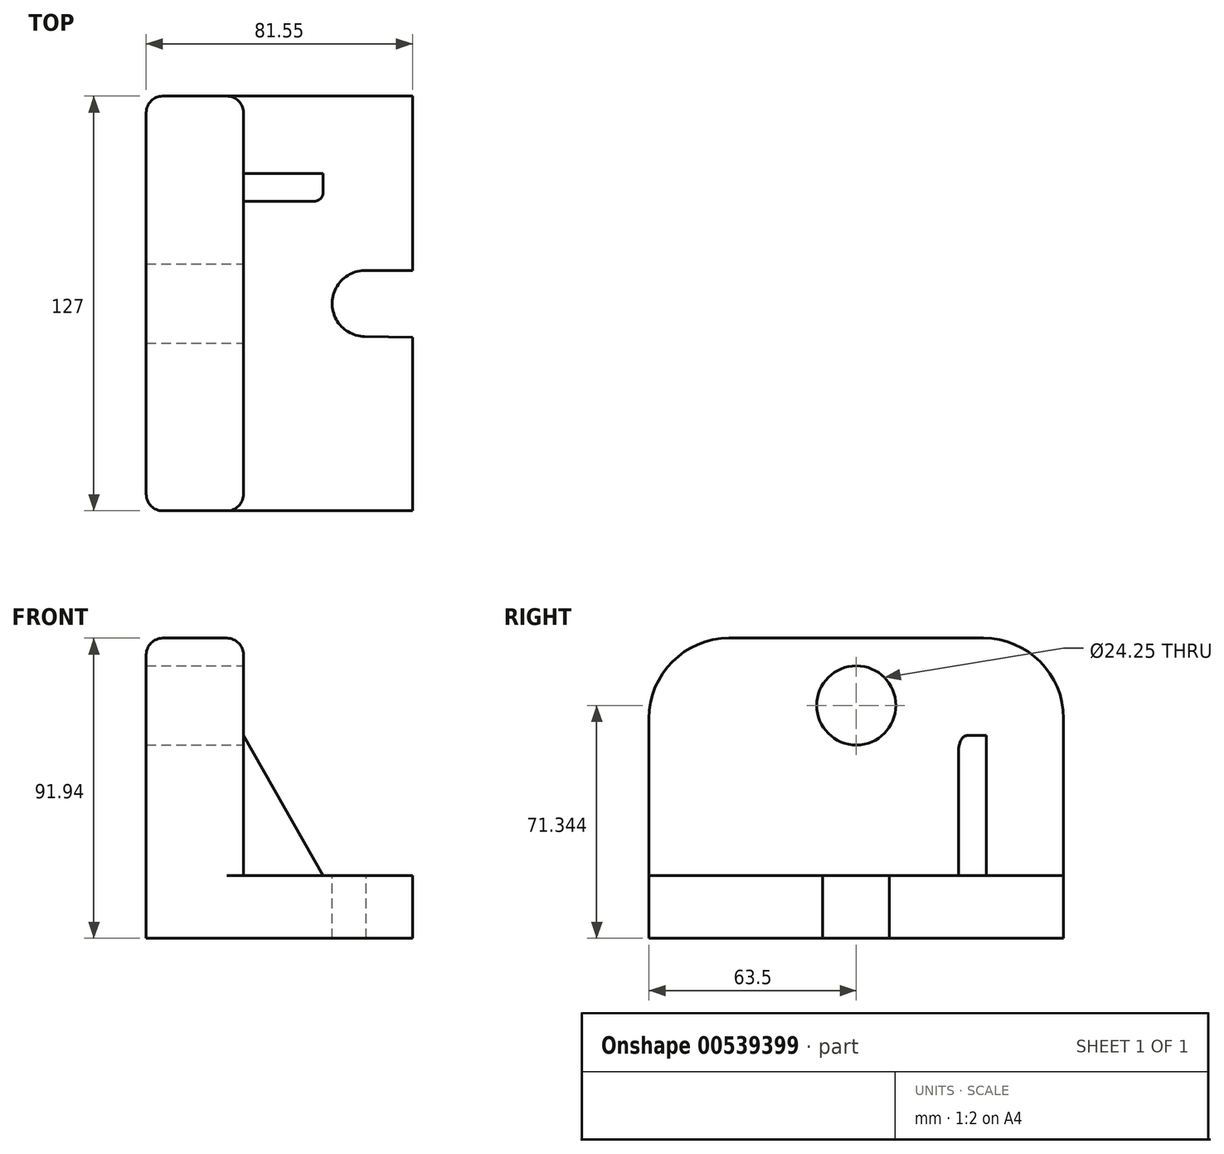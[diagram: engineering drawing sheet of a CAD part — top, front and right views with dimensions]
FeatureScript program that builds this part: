
annotation { "Feature Type Name" : "Feature", "Feature Type Description" : "" }
export const myFeature = defineFeature(function(context is Context, id is Id, definition is map)
    precondition{}
    {
        {
            var Q0;
            Q0=qCreatedBy(makeId("Front.planeOp"),FACE);
            var sketch = newSketch(context, id + "F0", { "sketchPlane" : qUnion([Q0])});
            skLineSegment(sketch, "E0", {"start": v(0, -21.47) * mm, "end": v(51.77, -21.47) * mm});
            skLineSegment(sketch, "E1", {"start": v(51.77, -21.47) * mm, "end": v(51.77, -40.63) * mm});
            skLineSegment(sketch, "E2", {"start": v(51.77, -40.63) * mm, "end": v(-29.78, -40.63) * mm});
            skLineSegment(sketch, "E3", {"start": v(-29.78, -40.63) * mm, "end": v(-29.78, 51.3) * mm});
            skLineSegment(sketch, "E4", {"start": v(-29.78, 51.3) * mm, "end": v(0, 51.3) * mm});
            skLineSegment(sketch, "E5", {"start": v(0, 51.3) * mm, "end": v(0, -21.47) * mm});
            skSolve(sketch);
        }
        {
            var Q0;
            Q0 = qSketchRegion(id + "F0", true);
            extrude(context, id + "F1", {"entities" : qUnion([Q0]), "endBound" : BoundingType.SYMMETRIC, "oppositeDirection" : true, "depth" : 127 * mm, "offsetDistance" : 25.4 * mm});
        }
        {
            var Q0;
            Q0=makeQuery(id+"F1.opExtrude","SWEPT_FACE",FACE,{"disambiguationData":[OSD([sQuery(id+"F0.wireOp",EDGE,"E0")])]});
            var sketch = newSketch(context, id + "F2", { "sketchPlane" : qUnion([Q0])});
            skPoint(sketch, "E6.centerSnap0", {"position": v(51.77, 0) * mm});
            skCircle(sketch, "E7", {"center": v(37.28, 0) * mm, "radius": 10.1 * mm});
            skLineSegment(sketch, "E8", {"start": v(36.9, 10.1) * mm, "end": v(51.77, 10.1) * mm});
            skLineSegment(sketch, "E9", {"start": v(37.13, -10.1) * mm, "end": v(51.77, -10.32) * mm});
            skSolve(sketch);
        }
        {
            var Q0;
            Q0 = qSketchRegion(id + "F2", true);
            var Q1;
            {var subQ0=sQuery(id+"F2.wireOp",EDGE,"E9");Q1=makeQuery(id+"F2.imprint","IMPRINT",FACE,{"disambiguationData":[TD([[makeQuery(id+"F2.imprint","IMPRINT",EDGE,{"derivedFrom":subQ0}),1.0]])]});}
            extrude(context, id + "F3", {"entities" : qUnion([Q0, Q1]), "operationType" : NewBodyOperationType.REMOVE, "oppositeDirection" : true, "depth" : 79.5 * mm, "offsetDistance" : 25.4 * mm});
        }
        {
            var Q0;
            Q0=makeQuery(id+"F1.opExtrude","CAP_EDGE",EDGE,{"disambiguationData":[OSD([sQuery(id+"F0.wireOp",EDGE,"E4")])],"isStart":true});
            var Q1;
            Q1=makeQuery(id+"F1.opExtrude","CAP_EDGE",EDGE,{"disambiguationData":[OSD([sQuery(id+"F0.wireOp",EDGE,"E4")])],"isStart":false});
            fillet(context, id + "F4", {"entities" : qUnion([Q0, Q1]), "radius" : 24.53 * mm, "tangentPropagation" : true, "allowEdgeOverflow" : false});
        }
        {
            var Q0;
            Q0=makeQuery(id+"F1.opExtrude","SWEPT_EDGE",EDGE,{"disambiguationData":[OSD([sQuery(id+"F0.wireOp",EDGE,"E4"),sQuery(id+"F0.wireOp",EDGE,"E5")])]});
            var Q1;
            Q1=makeQuery(id+"F1.opExtrude","SWEPT_EDGE",EDGE,{"disambiguationData":[OSD([sQuery(id+"F0.wireOp",EDGE,"E3"),sQuery(id+"F0.wireOp",EDGE,"E4")])]});
            fillet(context, id + "F5", {"entities" : qUnion([Q0, Q1]), "radius" : 5.08 * mm, "tangentPropagation" : true, "allowEdgeOverflow" : false});
        }
        {
            var Q0;
            Q0=qCreatedBy(makeId("Right.planeOp"),FACE);
            var sketch = newSketch(context, id + "F6", { "sketchPlane" : qUnion([Q0])});
            skCircle(sketch, "E10", {"center": v(0, 30.71) * mm, "radius": 12.13 * mm});
            skSolve(sketch);
        }
        {
            var Q0;
            Q0 = qSketchRegion(id + "F6", true);
            extrude(context, id + "F7", {"entities" : qUnion([Q0]), "operationType" : NewBodyOperationType.REMOVE, "oppositeDirection" : true, "depth" : 116.84 * mm, "offsetDistance" : 25.4 * mm});
        }
        {
            var Q0;
            Q0=makeQuery(id+"F1.opExtrude","SWEPT_FACE",FACE,{"disambiguationData":[OSD([sQuery(id+"F0.wireOp",EDGE,"E5")])]});
            var sketch = newSketch(context, id + "F8", { "sketchPlane" : qUnion([Q0])});
            skLineSegment(sketch, "E11.bottom", {"start": v(39.8, -21.47) * mm, "end": v(31.3, -21.47) * mm});
            skLineSegment(sketch, "E11.top", {"start": v(39.8, 21.47) * mm, "end": v(31.3, 21.47) * mm});
            skLineSegment(sketch, "E11.left", {"start": v(39.8, -21.47) * mm, "end": v(39.8, 21.47) * mm});
            skLineSegment(sketch, "E11.right", {"start": v(31.3, -21.47) * mm, "end": v(31.3, 21.47) * mm});
            skPoint(sketch, "E11.middle", {"position": v(35.54, 0) * mm});
            skLineSegment(sketch, "E12.MirrorCS", {"start": v(-31.3, -21.47) * mm, "end": v(-31.3, 21.47) * mm});
            skLineSegment(sketch, "E13.MirrorCS", {"start": v(-39.8, -21.47) * mm, "end": v(-39.8, 21.47) * mm});
            skLineSegment(sketch, "E14.MirrorCS", {"start": v(-39.8, 21.47) * mm, "end": v(-31.3, 21.47) * mm});
            skSolve(sketch);
        }
        {
            var Q0;
            Q0 = qSketchRegion(id + "F8", true);
            extrude(context, id + "F9", {"entities" : qUnion([Q0]), "operationType" : NewBodyOperationType.ADD, "depth" : 24.38 * mm, "offsetDistance" : 25.4 * mm});
        }
        {
            var Q0;
            Q0=makeQuery(id+"F9.opExtrude","SWEPT_FACE",FACE,{"disambiguationData":[OSD([sQuery(id+"F8.wireOp",EDGE,"E11.left")])]});
            var sketch = newSketch(context, id + "F10", { "sketchPlane" : qUnion([Q0])});
            skLineSegment(sketch, "E15", {"start": v(0, 21.47) * mm, "end": v(-24.38, -21.47) * mm});
            skSolve(sketch);
        }
        {
            var Q0;
            Q0=makeQuery(id+"F10.imprint","IMPRINT",FACE,{"disambiguationData":[TD([[makeQuery(id+"F10.imprint","IMPRINT",EDGE,{"derivedFrom":sQuery(id+"F10.wireOp",EDGE,"E15")}),-1.0]])]});
            extrude(context, id + "F11", {"entities" : qUnion([Q0]), "operationType" : NewBodyOperationType.REMOVE, "oppositeDirection" : true, "depth" : 99.82 * mm, "offsetDistance" : 25.4 * mm});
        }
        {
            var Q0;
            Q0=makeQuery(id+"F9.opExtrude","CAP_EDGE",EDGE,{"disambiguationData":[OSD([sQuery(id+"F8.wireOp",EDGE,"E11.left")])],"isStart":true});
            var Q1;
            Q1=makeQuery(id+"F11.boolean.opBoolean","COPY",EDGE,{"derivedFrom":makeQuery(id+"F11.opExtrude","CAP_EDGE",EDGE,{"disambiguationData":[OSD([sQuery(id+"F10.wireOp",EDGE,"E15")])],"isStart":true})});
            var Q2;
            Q2=makeQuery(id+"F9.opExtrude","SWEPT_EDGE",EDGE,{"disambiguationData":[OSD([sQuery(id+"F0.wireOp",EDGE,"E0"),sQuery(id+"F0.wireOp",EDGE,"E5"),sQuery(id+"F8.wireOp",EDGE,"E11.bottom"),sQuery(id+"F8.wireOp",EDGE,"E11.left")])]});
            var Q3;
            Q3=makeQuery(id+"F11.boolean.opBoolean","INTERSECT",EDGE,{"derivedFrom":[makeQuery(id+"F9.opExtrude","SWEPT_FACE",FACE,{"disambiguationData":[OSD([sQuery(id+"F8.wireOp",EDGE,"E11.right")])]}),makeQuery(id+"F11.opExtrude","SWEPT_FACE",FACE,{"disambiguationData":[OSD([sQuery(id+"F10.wireOp",EDGE,"E15")])]})]});
            var Q4;
            Q4=makeQuery(id+"F9.opExtrude","SWEPT_EDGE",EDGE,{"disambiguationData":[OSD([sQuery(id+"F0.wireOp",EDGE,"E0"),sQuery(id+"F0.wireOp",EDGE,"E5"),sQuery(id+"F8.wireOp",EDGE,"E11.bottom"),sQuery(id+"F8.wireOp",EDGE,"E11.right")])]});
            fillet(context, id + "F12", {"entities" : qUnion([Q0, Q1, Q2, Q3, Q4]), "radius" : 2.54 * mm, "tangentPropagation" : true, "allowEdgeOverflow" : false});
        }
    });
